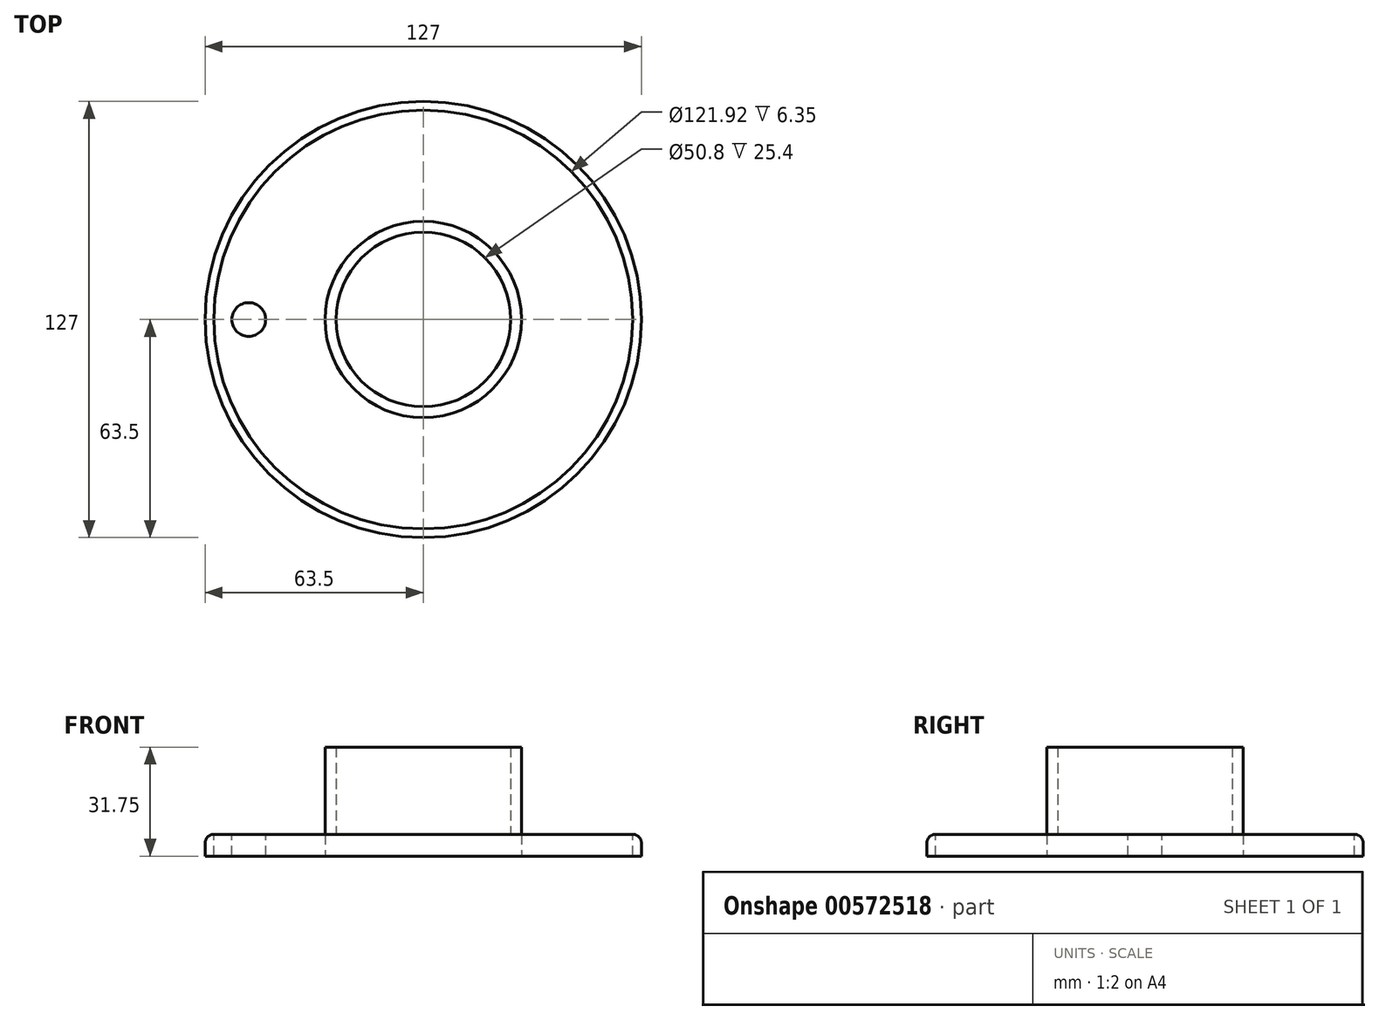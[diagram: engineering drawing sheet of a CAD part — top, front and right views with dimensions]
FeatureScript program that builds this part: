
annotation { "Feature Type Name" : "Feature", "Feature Type Description" : "" }
export const myFeature = defineFeature(function(context is Context, id is Id, definition is map)
    precondition{}
    {
        {
            var Q0;
            Q0=qCreatedBy(makeId("Top.planeOp"),FACE);
            var sketch = newSketch(context, id + "F0", { "sketchPlane" : qUnion([Q0])});
            skCircle(sketch, "E0", {"center": v(0, 0) * mm, "radius": 28.58 * mm});
            skCircle(sketch, "E1", {"center": v(0, 0) * mm, "radius": 25.4 * mm});
            skSolve(sketch);
        }
        {
            var Q0;
            Q0 = qSketchRegion(id + "F0", true);
            extrude(context, id + "F1", {"entities" : qUnion([Q0]), "depth" : 25.4 * mm, "offsetDistance" : 25.4 * mm});
        }
        {
            var Q0;
            Q0=qCreatedBy(makeId("Top.planeOp"),FACE);
            var sketch = newSketch(context, id + "F2", { "sketchPlane" : qUnion([Q0])});
            skCircle(sketch, "E2", {"center": v(0, 0) * mm, "radius": 63.5 * mm});
            skSolve(sketch);
        }
        {
            var Q0;
            Q0 = qSketchRegion(id + "F2", true);
            extrude(context, id + "F3", {"entities" : qUnion([Q0]), "operationType" : NewBodyOperationType.ADD, "oppositeDirection" : true, "depth" : 6.35 * mm, "offsetDistance" : 25.4 * mm});
        }
        {
            var Q0;
            Q0=makeQuery(id+"F3.opExtrude","CAP_EDGE",EDGE,{"disambiguationData":[OSD([sQuery(id+"F2.wireOp",EDGE,"E2")])],"isStart":true});
            var Q1;
            Q1=makeQuery(id+"F1.opExtrude","CAP_EDGE",EDGE,{"disambiguationData":[OSD([sQuery(id+"F0.wireOp",EDGE,"E0")])],"isStart":true});
            fillet(context, id + "F4", {"entities" : qUnion([Q0, Q1]), "radius" : 2.54 * mm, "tangentPropagation" : true, "allowEdgeOverflow" : false});
        }
        {
            var Q0;
            {var subQ0=sQuery(id+"F2.wireOp",EDGE,"E2");Q0=makeQuery(id+"F3.boolean.opBoolean","SPLIT",FACE,{"disambiguationData":[TD([makeQuery(id+"F1.opExtrude","SWEPT_FACE",FACE,{"disambiguationData":[OSD([sQuery(id+"F0.wireOp",EDGE,"E0")])]})])],"derivedFrom":makeQuery(id+"F3.opExtrude","CAP_FACE",FACE,{"disambiguationData":[OSD([subQ0])],"isStart":true})});}
            var sketch = newSketch(context, id + "F5", { "sketchPlane" : qUnion([Q0])});
            skCircle(sketch, "E3", {"center": v(0, 0) * mm, "radius": 50.8 * mm, "construction": true});
            skCircle(sketch, "E4", {"center": v(50.8, 0) * mm, "radius": 4.92 * mm});
            skLineSegment(sketch, "E5", {"start": v(0, 0) * mm, "end": v(0, -91.95) * mm, "construction": true});
            skLineSegment(sketch, "E6", {"start": v(0, -91.95) * mm, "end": v(0, 98.73) * mm, "construction": true});
            skCircle(sketch, "E7.MirrorC", {"center": v(-50.8, 0) * mm, "radius": 4.92 * mm});
            skCircle(sketch, "E8", {"center": v(0, -50.8) * mm, "radius": 4.92 * mm});
            skCircle(sketch, "E9", {"center": v(0, 50.8) * mm, "radius": 4.92 * mm});
            skSolve(sketch);
        }
        {
            var Q0;
            Q0=makeQuery(id+"F5.imprint","IMPRINT",FACE,{"disambiguationData":[TD([[makeQuery(id+"F5.imprint","IMPRINT",EDGE,{"derivedFrom":sQuery(id+"F5.wireOp",EDGE,"E4")}),1.0]])]});
            var Q1;
            Q1=makeQuery(id+"F5.imprint","IMPRINT",FACE,{"disambiguationData":[TD([[makeQuery(id+"F5.imprint","IMPRINT",EDGE,{"derivedFrom":sQuery(id+"F5.wireOp",EDGE,"E8")}),1.0]])]});
            var Q2;
            Q2=makeQuery(id+"F5.imprint","IMPRINT",FACE,{"disambiguationData":[TD([[makeQuery(id+"F5.imprint","IMPRINT",EDGE,{"derivedFrom":sQuery(id+"F5.wireOp",EDGE,"E7.MirrorC")}),-1.0]])]});
            var Q3;
            Q3=makeQuery(id+"F5.imprint","IMPRINT",FACE,{"disambiguationData":[TD([[makeQuery(id+"F5.imprint","IMPRINT",EDGE,{"derivedFrom":sQuery(id+"F5.wireOp",EDGE,"E9")}),1.0]])]});
            var Q4;
            Q4=sQuery(id+"F5.wireOp",EDGE,"E4");
            extrude(context, id + "F6", {"entities" : qUnion([Q0, Q1, Q2, Q3]), "operationType" : NewBodyOperationType.REMOVE, "surfaceEntities" : qUnion([Q4]), "endBound" : BoundingType.UP_TO_NEXT, "oppositeDirection" : true, "depth" : 25.4 * mm, "offsetDistance" : 25.4 * mm});
        }
    });
